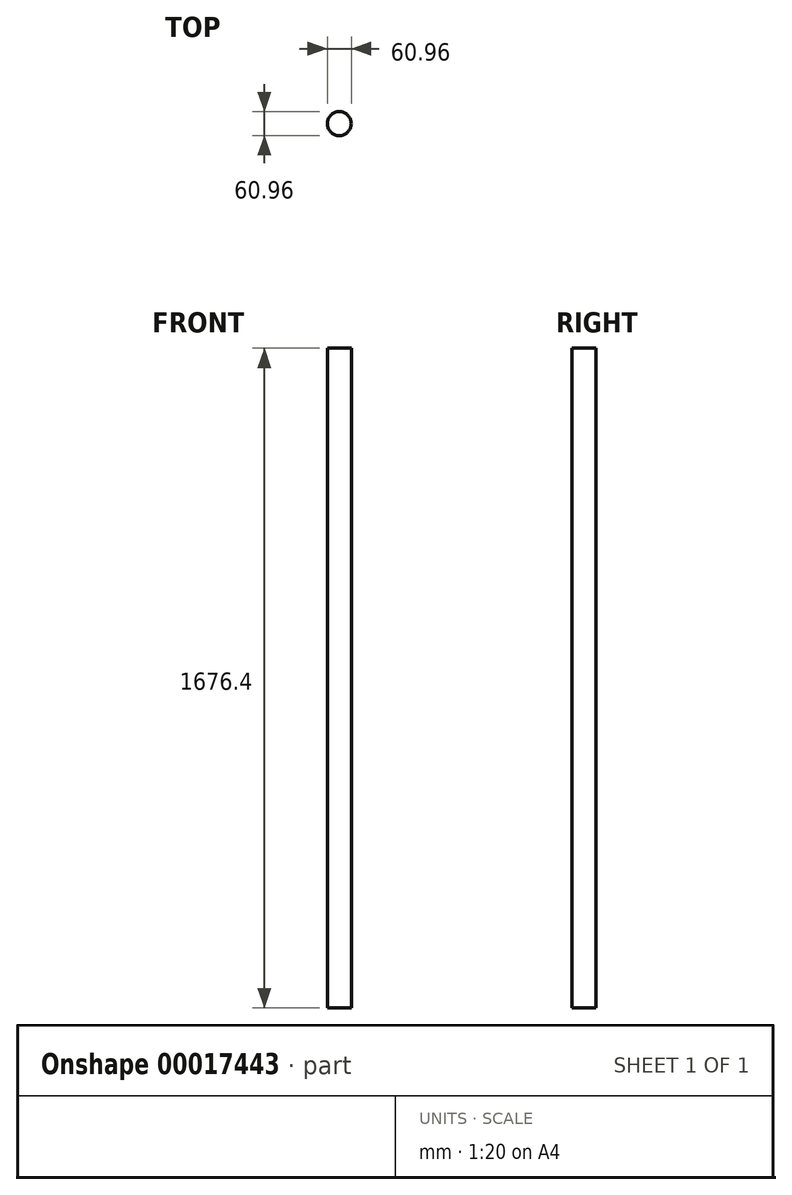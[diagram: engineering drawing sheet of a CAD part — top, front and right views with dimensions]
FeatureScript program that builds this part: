
annotation { "Feature Type Name" : "Feature", "Feature Type Description" : "" }
export const myFeature = defineFeature(function(context is Context, id is Id, definition is map)
    precondition{}
    {
        {
            var Q0;
            Q0=qCreatedBy(makeId("Top.planeOp"),FACE);
            var sketch = newSketch(context, id + "F0", { "sketchPlane" : qUnion([Q0])});
            skCircle(sketch, "E0", {"center": v(0, 0) * mm, "radius": 30.48 * mm});
            skSolve(sketch);
        }
        {
            var Q0;
            Q0=makeQuery(id+"F0.imprint","IMPRINT",FACE,{"disambiguationData":[TD([[makeQuery(id+"F0.imprint","IMPRINT",EDGE,{"derivedFrom":sQuery(id+"F0.wireOp",EDGE,"E0")}),1.0]])]});
            extrude(context, id + "F1", {"entities" : qUnion([Q0]), "depth" : 1219.2 * mm, "hasSecondDirection" : true, "secondDirectionOppositeDirection" : true, "secondDirectionDepth" : 457.2 * mm});
        }
    });
